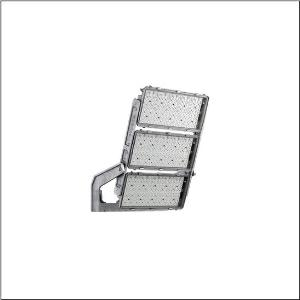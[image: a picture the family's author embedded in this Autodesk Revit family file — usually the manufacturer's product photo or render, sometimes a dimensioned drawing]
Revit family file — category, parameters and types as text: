
# Revit family: floodlight_fl_11_maxi_pro_remote___pl33t_5xa779424t01aa_a9ee
name_source: partatom
category: Lighting Fixtures
units: mm (PartAtom-declared; Revit-internal decimal feet)

## family parameters
Cut with Voids When Loaded = No
Host = Face
Light Source = No
Part Type = Normal
Room Calculation Point = No
Round Connector Dimension = Use Diameter
Shared = No

## types (1)
- --- (1 x LED, 164520 lm, 1539.3 W, 5700K)
    Apparent Load = 1539 VA
    CIE Flux Codes = 27 70 98 100 100
    Color Rendering = 90
    Color Temperature = 5700K
    Default Elevation = 1800 mm
    Description = Floodlight FL 11  maxi  pro Remote floodlight; light control with lens of PMMA; cover panel of toughened safety glass, transparent; light distribution: PL33T, asymmetric direct distribution, LEDcolour temperature: 5700K, rated luminous flux: 164.520lm, colour rendering: CRI > 90, light colour: 957; luminous efficacy: 107lm/W; brightness control: DALI 2 (1 DALI address); with terminal, 8-pole, max. 2.5mm², mains connection: 220..240V/380..400V AC, 50/60Hz, surge voltage resistance: line to ground: 10kV, ECG replaceable separately, no afterglow with DALI off / DMX off command, LED unit replaceable without ESD environment, dustproof LED module, dimming range 10..100%; 1539W floodlight with 3x LED unit of diecast aluminium, coated grey; length: 1.003mm / width: 651mm / height: 338mm; mounting bracket, of diecast aluminium, uncoated, natural, equipment: Power, protection rating (complete): IP66; insulation class (complete): insulation class I (protective earthing); certification: CE, ENEC, VDE; ball protection: ball impact resistant, impact resistance: IK07; only for outdoor installations, rated ambient temperature 10°C, permissible operating ambient temperature: -40..+30°C, permissible storage temperature: -40..+85°C; packaging unit: 1 piece

Light Distribution: PL33T
    Height = 320 mm
    Lamp = 1 x LED
    Lamp Light Flux = 164520 lm
    Lamp Power = 1539.3 W
    Lamp count = 1
    Length = 1002 mm
    Luminous efficacy = 107 lm/W
    Manufacturer = Siteco
    ModVariant = No
    Model = 5XA779424T01AA
    Mounting Place = Ceiling
    Mounting Type = Surface mounted
    Number of Poles = 1
    OnlyDefault = Yes
    Power Factor = 1
    Product Name = Floodlight FL 11 maxi pro Remote | PL33T
    Product group = floodlight | ceiling mounted
    ProductGroupID = 303
    Protection Class = Protection class I
    Protection Degree = IP 66
    RLX_Detail_Level = 1
    RLX_Emergency_Light_Flux = 0 lm
    RLX_Emergency_Type = 0
    RLX_Emergency_Type_DB = No
    RlxData = <blob elided: 52341 chars, md5=b37e5398>
    Socket = socket
    Standby Power = 0 W
    System Light Flux = 164520 lm
    System Power = 1539 W
    Type Comments = factory setting: luminous flux: 100 % | dim-lin: 254 | 1080 mA
    Type Image = l_1006784.jpg
    URL = http://relux.com
    VarID = @adj_030119
    Voltage = 0 V
    Weight = 0.00 kg
    Width = 655 mm

## geometry (parser evidence)
native form markers: Blend x4, Sweep x13
no freeform markers — native parametric forms only
